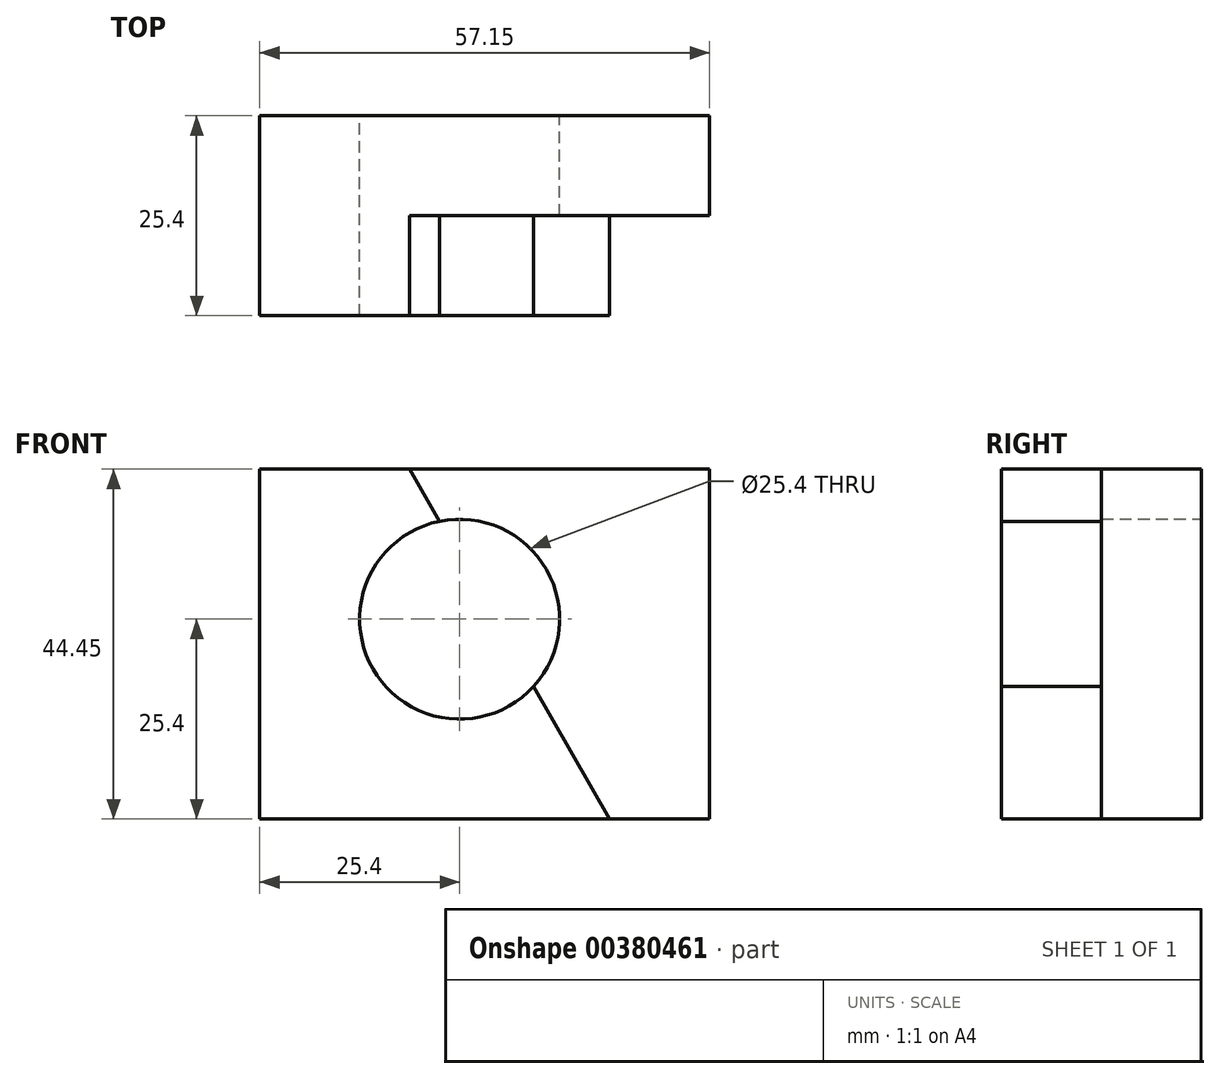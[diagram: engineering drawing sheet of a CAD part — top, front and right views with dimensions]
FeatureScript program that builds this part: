
annotation { "Feature Type Name" : "Feature", "Feature Type Description" : "" }
export const myFeature = defineFeature(function(context is Context, id is Id, definition is map)
    precondition{}
    {
        {
            var Q0;
            Q0=qCreatedBy(makeId("Front.planeOp"),FACE);
            var sketch = newSketch(context, id + "F0", { "sketchPlane" : qUnion([Q0])});
            skLineSegment(sketch, "E0", {"start": v(0, 0) * mm, "end": v(57.15, 0) * mm});
            skLineSegment(sketch, "E1", {"start": v(57.15, 0) * mm, "end": v(57.15, 44.45) * mm});
            skLineSegment(sketch, "E2", {"start": v(57.15, 44.45) * mm, "end": v(0, 44.45) * mm});
            skLineSegment(sketch, "E3", {"start": v(0, 44.45) * mm, "end": v(0, 0) * mm});
            skSolve(sketch);
        }
        {
            var Q0;
            Q0=makeQuery(id+"F0.imprint","IMPRINT",FACE,{"disambiguationData":[TD([[makeQuery(id+"F0.imprint","IMPRINT",EDGE,{"derivedFrom":sQuery(id+"F0.wireOp",EDGE,"E0")}),1.0]])]});
            extrude(context, id + "F1", {"entities" : qUnion([Q0]), "depth" : 25.4 * mm, "offsetDistance" : 25.4 * mm});
        }
        {
            var Q0;
            Q0=makeQuery(id+"F1.opExtrude","SWEPT_FACE",FACE,{"disambiguationData":[OSD([sQuery(id+"F0.wireOp",EDGE,"E2")])]});
            var sketch = newSketch(context, id + "F2", { "sketchPlane" : qUnion([Q0])});
            skLineSegment(sketch, "E4", {"start": v(19.05, -25.4) * mm, "end": v(19.05, -12.7) * mm});
            skLineSegment(sketch, "E5", {"start": v(19.05, -12.7) * mm, "end": v(57.15, -12.7) * mm});
            skSolve(sketch);
        }
        {
            var Q0;
            Q0 = qSketchRegion(id + "F2", true);
            var Q1;
            {var subQ0=sQuery(id+"F2.wireOp",EDGE,"E4");Q1=makeQuery(id+"F2.imprint","IMPRINT",FACE,{"disambiguationData":[TD([[makeQuery(id+"F2.imprint","IMPRINT",EDGE,{"derivedFrom":subQ0}),-1.0]])]});}
            extrude(context, id + "F3", {"entities" : qUnion([Q0, Q1]), "operationType" : NewBodyOperationType.REMOVE, "oppositeDirection" : true, "depth" : 44.45 * mm, "offsetDistance" : 25.4 * mm});
        }
        {
            var Q0;
            Q0=makeQuery(id+"F3.boolean.opBoolean","COPY",FACE,{"derivedFrom":makeQuery(id+"F3.opExtrude","SWEPT_FACE",FACE,{"disambiguationData":[OSD([sQuery(id+"F2.wireOp",EDGE,"E5")])]})});
            var sketch = newSketch(context, id + "F4", { "sketchPlane" : qUnion([Q0])});
            skLineSegment(sketch, "E6", {"start": v(19.05, 44.45) * mm, "end": v(44.45, 0) * mm});
            skSolve(sketch);
        }
        {
            var Q0;
            Q0 = qSketchRegion(id + "F4", true);
            var Q1;
            {var subQ0=sQuery(id+"F4.wireOp",EDGE,"E6");Q1=makeQuery(id+"F4.imprint","IMPRINT",FACE,{"disambiguationData":[TD([[makeQuery(id+"F4.imprint","IMPRINT",EDGE,{"derivedFrom":subQ0}),-1.0]])]});}
            extrude(context, id + "F5", {"entities" : qUnion([Q0, Q1]), "operationType" : NewBodyOperationType.ADD, "depth" : 12.7 * mm, "offsetDistance" : 25.4 * mm});
        }
        {
            var Q0;
            Q0=qCreatedBy(makeId("Front.planeOp"),FACE);
            var sketch = newSketch(context, id + "F6", { "sketchPlane" : qUnion([Q0])});
            skCircle(sketch, "E7", {"center": v(25.4, 25.4) * mm, "radius": 12.7 * mm});
            skSolve(sketch);
        }
        {
            var Q0;
            Q0 = qSketchRegion(id + "F6", true);
            extrude(context, id + "F7", {"entities" : qUnion([Q0]), "operationType" : NewBodyOperationType.REMOVE, "depth" : 41.66 * mm, "offsetDistance" : 25.4 * mm});
        }
    });
